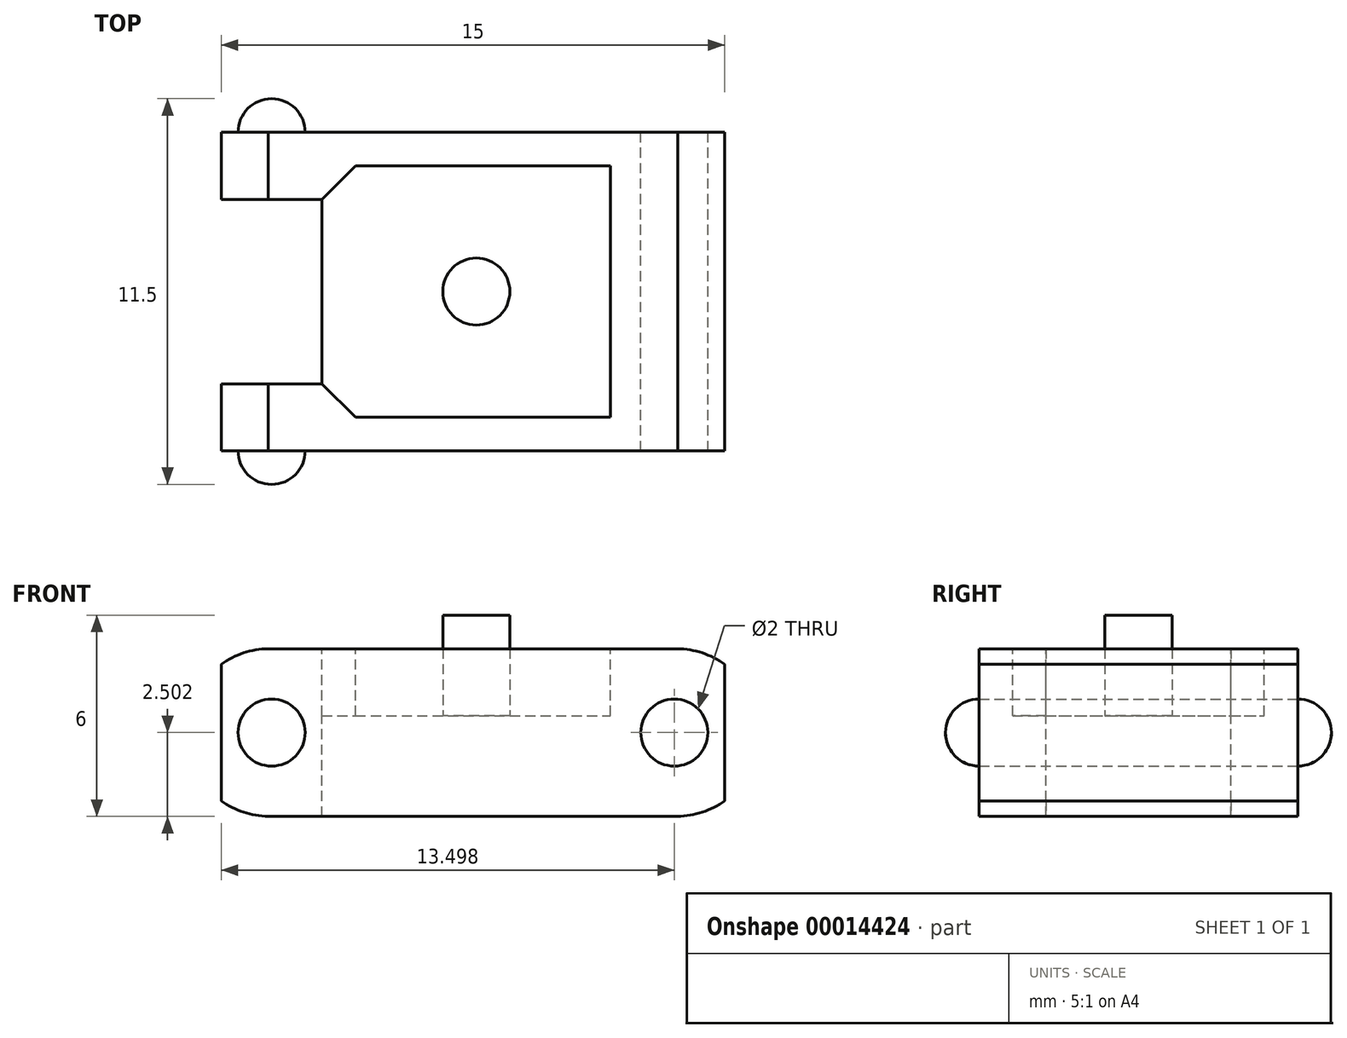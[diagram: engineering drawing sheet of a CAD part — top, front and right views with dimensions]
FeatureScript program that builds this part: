
annotation { "Feature Type Name" : "Feature", "Feature Type Description" : "" }
export const myFeature = defineFeature(function(context is Context, id is Id, definition is map)
    precondition{}
    {
        {
            var Q0;
            Q0=qCreatedBy(makeId("Front.planeOp"),FACE);
            var sketch = newSketch(context, id + "F0", { "sketchPlane" : qUnion([Q0])});
            skLineSegment(sketch, "E0.bottom", {"start": v(28.09, 13.2) * mm, "end": v(43.09, 13.2) * mm});
            skLineSegment(sketch, "E0.top", {"start": v(28.09, 8.2) * mm, "end": v(43.09, 8.2) * mm});
            skLineSegment(sketch, "E0.left", {"start": v(28.09, 13.2) * mm, "end": v(28.09, 8.2) * mm});
            skLineSegment(sketch, "E0.right", {"start": v(43.09, 13.2) * mm, "end": v(43.09, 8.2) * mm});
            skLineSegment(sketch, "E1", {"start": v(35.59, 8.2) * mm, "end": v(35.59, 13.2) * mm, "construction": true});
            skPoint(sketch, "E2", {"position": v(31.09, 13.2) * mm});
            skLineSegment(sketch, "E3", {"start": v(28.09, 8.2) * mm, "end": v(31.09, 13.2) * mm, "construction": true});
            skLineSegment(sketch, "E4", {"start": v(31.09, 13.2) * mm, "end": v(31.09, 8.2) * mm, "construction": true});
            skLineSegment(sketch, "E5", {"start": v(31.09, 8.2) * mm, "end": v(28.09, 13.2) * mm, "construction": true});
            skCircle(sketch, "E6", {"center": v(29.59, 10.7) * mm, "radius": 1 * mm});
            skLineSegment(sketch, "E7", {"start": v(29.59, 13.2) * mm, "end": v(29.59, 8.2) * mm, "construction": true});
            skLineSegment(sketch, "E8", {"start": v(28.09, 10.7) * mm, "end": v(31.09, 10.7) * mm, "construction": true});
            skArc(sketch, "E9", {"start": v(29.59, 13.2) * mm, "mid": v(27.04, 10.7) * mm, "end": v(29.59, 8.2) * mm});
            skCircle(sketch, "E10.0.MirrorC", {"center": v(41.59, 10.7) * mm, "radius": 1 * mm});
            skArc(sketch, "E11.0.MirrorCS", {"start": v(41.59, 13.2) * mm, "mid": v(44.14, 10.7) * mm, "end": v(41.59, 8.2) * mm});
            skSolve(sketch);
        }
        {
            var Q0;
            {var subQ5=sQuery(id+"F0.wireOp",EDGE,"E0.right");Q0=makeQuery(id+"F0.imprint","IMPRINT",FACE,{"disambiguationData":[TD([[makeQuery(id+"F0.imprint","IMPRINT",EDGE,{"derivedFrom":subQ5}),-1.0]])]});}
            var Q1;
            Q1=makeQuery(id+"F0.imprint","IMPRINT",FACE,{"disambiguationData":[TD([[makeQuery(id+"F0.imprint","IMPRINT",EDGE,{"derivedFrom":sQuery(id+"F0.wireOp",EDGE,"E6")}),-1.0]])]});
            var Q2;
            {var subQ5=sQuery(id+"F0.wireOp",EDGE,"E0.left");Q2=makeQuery(id+"F0.imprint","IMPRINT",FACE,{"disambiguationData":[TD([[makeQuery(id+"F0.imprint","IMPRINT",EDGE,{"derivedFrom":subQ5}),1.0]])]});}
            var Q3;
            Q3=makeQuery(id+"F0.imprint","IMPRINT",FACE,{"disambiguationData":[TD([[makeQuery(id+"F0.imprint","IMPRINT",EDGE,{"derivedFrom":sQuery(id+"F0.wireOp",EDGE,"E6")}),1.0]])]});
            var Q4;
            Q4=makeQuery(id+"F0.imprint","IMPRINT",FACE,{"disambiguationData":[TD([[makeQuery(id+"F0.imprint","IMPRINT",EDGE,{"derivedFrom":sQuery(id+"F0.wireOp",EDGE,"E10.0.MirrorC")}),-1.0]])]});
            extrude(context, id + "F1", {"entities" : qUnion([Q0, Q1, Q2, Q3, Q4]), "depth" : 9.5 * mm});
        }
        {
            var Q0;
            Q0=makeQuery(id+"F1.opExtrude","SWEPT_FACE",FACE,{"disambiguationData":[OSD([sQuery(id+"F0.wireOp",EDGE,"E0.bottom")])]});
            var sketch = newSketch(context, id + "F2", { "sketchPlane" : qUnion([Q0])});
            skLineSegment(sketch, "E12", {"start": v(35.59, 0) * mm, "end": v(35.59, -9.5) * mm, "construction": true});
            skLineSegment(sketch, "E13", {"start": v(28.09, -4.75) * mm, "end": v(43.09, -4.75) * mm, "construction": true});
            skPoint(sketch, "E14", {"position": v(31.09, 0) * mm});
            skLineSegment(sketch, "E15", {"start": v(31.09, 0) * mm, "end": v(31.09, -9.5) * mm, "construction": true});
            skPoint(sketch, "E16", {"position": v(28.09, -2) * mm});
            skLineSegment(sketch, "E17", {"start": v(28.09, -2) * mm, "end": v(31.09, -2) * mm});
            skLineSegment(sketch, "E18.0.MirrorCS", {"start": v(28.09, -7.5) * mm, "end": v(31.09, -7.5) * mm});
            skLineSegment(sketch, "E19", {"start": v(31.09, -7.5) * mm, "end": v(31.09, -2) * mm});
            skLineSegment(sketch, "E20", {"start": v(28.09, -2) * mm, "end": v(28.09, -7.5) * mm});
            skSolve(sketch);
        }
        {
            var Q0;
            Q0=makeQuery(id+"F2.imprint","IMPRINT",FACE,{"disambiguationData":[TD([[makeQuery(id+"F2.imprint","IMPRINT",EDGE,{"derivedFrom":sQuery(id+"F2.wireOp",EDGE,"E17")}),-1.0]])]});
            var Q1;
            Q1=makeQuery(id+"F2.imprint","IMPRINT",FACE,{"disambiguationData":[TD([[makeQuery(id+"F2.imprint","IMPRINT",EDGE,{"derivedFrom":sQuery(id+"F2.wireOp",EDGE,"8c34fa15-d911-4d8d-b620-4605c3a337e2.0.MirrorCS")}),-1.0]])]});
            extrude(context, id + "F3", {"entities" : qUnion([Q0, Q1]), "operationType" : NewBodyOperationType.REMOVE, "endBound" : BoundingType.THROUGH_ALL, "oppositeDirection" : true, "depth" : 25 * mm});
        }
        {
            var Q0;
            {var subQ5=sQuery(id+"F0.wireOp",EDGE,"E0.right");Q0=makeQuery(id+"F0.imprint","IMPRINT",FACE,{"disambiguationData":[TD([[makeQuery(id+"F0.imprint","IMPRINT",EDGE,{"derivedFrom":subQ5}),-1.0]])]});}
            var Q1;
            {var subQ5=sQuery(id+"F0.wireOp",EDGE,"E0.left");Q1=makeQuery(id+"F0.imprint","IMPRINT",FACE,{"disambiguationData":[TD([[makeQuery(id+"F0.imprint","IMPRINT",EDGE,{"derivedFrom":subQ5}),1.0]])]});}
            extrude(context, id + "F4", {"entities" : qUnion([Q0, Q1]), "operationType" : NewBodyOperationType.REMOVE, "endBound" : BoundingType.THROUGH_ALL, "depth" : 25 * mm});
        }
        {
            var Q0;
            Q0=makeQuery(id+"F0.imprint","IMPRINT",FACE,{"disambiguationData":[TD([[makeQuery(id+"F0.imprint","IMPRINT",EDGE,{"derivedFrom":sQuery(id+"F0.wireOp",EDGE,"E6")}),1.0]])]});
            extrude(context, id + "F5", {"entities" : qUnion([Q0]), "operationType" : NewBodyOperationType.ADD, "oppositeDirection" : true, "depth" : 1 * mm});
        }
        {
            var Q0;
            Q0=makeQuery(id+"F1.opExtrude","CAP_FACE",FACE,{"disambiguationData":[OSD([sQuery(id+"F0.wireOp",EDGE,"E0.bottom"),sQuery(id+"F0.wireOp",EDGE,"E0.top"),sQuery(id+"F0.wireOp",EDGE,"E0.left"),sQuery(id+"F0.wireOp",EDGE,"E0.right")])],"isStart":false});
            var sketch = newSketch(context, id + "F6", { "sketchPlane" : qUnion([Q0])});
            skLineSegment(sketch, "E21", {"start": v(35.59, 8.2) * mm, "end": v(35.59, 13.2) * mm, "construction": true});
            skPoint(sketch, "E22", {"position": v(31.09, 8.2) * mm});
            skPoint(sketch, "E23", {"position": v(28.09, 8.2) * mm});
            skLineSegment(sketch, "E24", {"start": v(31.09, 8.2) * mm, "end": v(31.09, 13.2) * mm, "construction": true});
            skLineSegment(sketch, "E25", {"start": v(31.09, 13.2) * mm, "end": v(28.09, 8.2) * mm, "construction": true});
            skPoint(sketch, "E26", {"position": v(28.09, 13.2) * mm});
            skLineSegment(sketch, "E27", {"start": v(28.09, 13.2) * mm, "end": v(28.09, 8.2) * mm, "construction": true});
            skLineSegment(sketch, "E28", {"start": v(31.09, 13.2) * mm, "end": v(28.09, 13.2) * mm, "construction": true});
            skLineSegment(sketch, "E29", {"start": v(28.09, 13.2) * mm, "end": v(31.09, 8.2) * mm, "construction": true});
            skCircle(sketch, "E30", {"center": v(29.59, 10.7) * mm, "radius": 1 * mm});
            skCircle(sketch, "E31.MirrorC", {"center": v(41.59, 10.7) * mm, "radius": 1 * mm});
            skSolve(sketch);
        }
        {
            var Q0;
            Q0=makeQuery(id+"F6.imprint","IMPRINT",FACE,{"disambiguationData":[TD([[makeQuery(id+"F6.imprint","IMPRINT",EDGE,{"derivedFrom":sQuery(id+"F6.wireOp",EDGE,"E30")}),1.0]])]});
            extrude(context, id + "F7", {"entities" : qUnion([Q0]), "operationType" : NewBodyOperationType.ADD, "depth" : 1 * mm, "hasSecondDirectionDraft" : true, "secondDirectionDraftAngle" : 10 * degree});
        }
        {
            var Q0;
            Q0=makeQuery(id+"F1.opExtrude","SWEPT_FACE",FACE,{"disambiguationData":[OSD([sQuery(id+"F0.wireOp",EDGE,"E0.bottom")])]});
            var sketch = newSketch(context, id + "F8", { "sketchPlane" : qUnion([Q0])});
            skPoint(sketch, "E32", {"position": v(31.09, -2) * mm});
            skPoint(sketch, "E33", {"position": v(31.09, -4.75) * mm});
            skLineSegment(sketch, "E34", {"start": v(31.09, -4.75) * mm, "end": v(41.69, -4.75) * mm, "construction": true});
            skPoint(sketch, "E35", {"position": v(39.69, -4.75) * mm});
            skLineSegment(sketch, "E36", {"start": v(31.09, -2) * mm, "end": v(41.69, -2) * mm, "construction": true});
            skLineSegment(sketch, "E37", {"start": v(39.69, -4.75) * mm, "end": v(39.69, -2) * mm});
            skLineSegment(sketch, "E38", {"start": v(31.09, -4.75) * mm, "end": v(31.09, -2) * mm});
            skLineSegment(sketch, "E39.MirrorCS", {"start": v(31.09, -4.75) * mm, "end": v(31.09, -7.5) * mm});
            skLineSegment(sketch, "E40.MirrorCS", {"start": v(39.69, -4.75) * mm, "end": v(39.69, -7.5) * mm});
            skPoint(sketch, "E41", {"position": v(41.69, -1) * mm});
            skPoint(sketch, "E42", {"position": v(41.69, 0) * mm});
            skLineSegment(sketch, "E43", {"start": v(41.69, -1) * mm, "end": v(31.09, -1) * mm, "construction": true});
            skPoint(sketch, "E44", {"position": v(32.09, -1) * mm});
            skLineSegment(sketch, "E45", {"start": v(31.09, -2) * mm, "end": v(31.09, -1) * mm, "construction": true});
            skLineSegment(sketch, "E46", {"start": v(31.09, -2) * mm, "end": v(32.09, -1) * mm});
            skPoint(sketch, "E47", {"position": v(39.69, -1) * mm});
            skLineSegment(sketch, "E48", {"start": v(32.09, -1) * mm, "end": v(39.69, -1) * mm});
            skLineSegment(sketch, "E49", {"start": v(39.69, -1) * mm, "end": v(39.69, -2) * mm});
            skLineSegment(sketch, "E50.MirrorCS", {"start": v(31.09, -7.5) * mm, "end": v(32.09, -8.5) * mm});
            skLineSegment(sketch, "E51.MirrorCS", {"start": v(32.09, -8.5) * mm, "end": v(39.69, -8.5) * mm});
            skLineSegment(sketch, "E52.MirrorCS", {"start": v(39.69, -8.5) * mm, "end": v(39.69, -7.5) * mm});
            skPoint(sketch, "E53.MirrorCS.end.orphan", {"position": v(31.09, -7.5) * mm});
            skPoint(sketch, "E53.MirrorCS.start.orphan", {"position": v(39.69, -7.5) * mm});
            skSolve(sketch);
        }
        {
            var Q0;
            Q0=makeQuery(id+"F8.imprint","IMPRINT",FACE,{"disambiguationData":[TD([[makeQuery(id+"F8.imprint","IMPRINT",EDGE,{"derivedFrom":sQuery(id+"F8.wireOp",EDGE,"E37")}),1.0]])]});
            extrude(context, id + "F9", {"entities" : qUnion([Q0]), "operationType" : NewBodyOperationType.REMOVE, "oppositeDirection" : true, "depth" : 2 * mm});
        }
        {
            var Q0;
            Q0=makeQuery(id+"F9.boolean.opBoolean","COPY",FACE,{"derivedFrom":makeQuery(id+"F9.opExtrude","CAP_FACE",FACE,{"disambiguationData":[OSD([sQuery(id+"F8.wireOp",EDGE,"E37"),sQuery(id+"F8.wireOp",EDGE,"1d8b683b-c03d-4aed-a5cb-2ff89669d674"),sQuery(id+"F8.wireOp",EDGE,"E38"),sQuery(id+"F8.wireOp",EDGE,"E53.MirrorCS"),sQuery(id+"F8.wireOp",EDGE,"E39.MirrorCS"),sQuery(id+"F8.wireOp",EDGE,"E40.MirrorCS")])],"isStart":false})});
            var sketch = newSketch(context, id + "F10", { "sketchPlane" : qUnion([Q0])});
            skPoint(sketch, "E54", {"position": v(31.09, -4.75) * mm});
            skPoint(sketch, "E55", {"position": v(39.69, -4.75) * mm});
            skLineSegment(sketch, "E56", {"start": v(31.09, -4.75) * mm, "end": v(39.69, -4.75) * mm, "construction": true});
            skPoint(sketch, "E57", {"position": v(35.69, -4.75) * mm});
            skPoint(sketch, "E58", {"position": v(32.83, -4.75) * mm});
            skCircle(sketch, "E59", {"center": v(35.69, -4.75) * mm, "radius": 1 * mm});
            skSolve(sketch);
        }
        {
            var Q0;
            Q0=makeQuery(id+"F5.opExtrude","CAP_EDGE",EDGE,{"disambiguationData":[OSD([sQuery(id+"F0.wireOp",EDGE,"E6")])],"isStart":false});
            var Q1;
            Q1=makeQuery(id+"F7.opExtrude","CAP_EDGE",EDGE,{"disambiguationData":[OSD([sQuery(id+"F6.wireOp",EDGE,"E30")])],"isStart":false});
            fillet(context, id + "F11", {"entities" : qUnion([Q0, Q1]), "radius" : 1 * mm, "tangentPropagation" : true, "allowEdgeOverflow" : false});
        }
        {
            var Q0;
            Q0=makeQuery(id+"F10.imprint","IMPRINT",FACE,{"disambiguationData":[TD([[makeQuery(id+"F10.imprint","IMPRINT",EDGE,{"derivedFrom":sQuery(id+"F10.wireOp",EDGE,"E59")}),1.0]])]});
            extrude(context, id + "F12", {"entities" : qUnion([Q0]), "operationType" : NewBodyOperationType.ADD, "depth" : 3 * mm});
        }
    });
